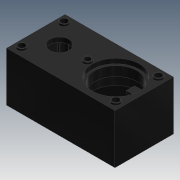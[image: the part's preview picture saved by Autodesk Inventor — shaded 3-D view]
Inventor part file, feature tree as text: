
AUTODESK INVENTOR PART (.ipt)
format: ipt  version: 2017 (Build 210142000, 142)  size: 245,760 bytes
history: native  units: mm
features: sketch x14, extrude x11, hole x3, projected_geometry x3, other x1, chamfer x1
ambient origin geometry x8: Origin, YZ Plane, XZ Plane, XY Plane, X Axis, Y Axis, Z Axis, Center Point
bodies: Body1 (feature_tree)
feature tree (33):
  other  "Твердое тело1"
  extrude  "Выдавливание1"  Depth=12.4mm
  extrude  "Выдавливание2"  Depth=23.0mm
  chamfer  "Фаска1"  Distance=10.5mm
  extrude  "Выдавливание3"  Depth=9.5mm TaperAngle=0.0deg
  extrude  "Выдавливание4"  Depth=1.5mm TaperAngle=45.0deg
  hole  "Отверстие1"  [1 undecoded]
  extrude  "Выдавливание5"  Depth=8.0mm
  extrude  "Выдавливание6"  Depth=1.0mm
  extrude  "Выдавливание7"  Depth=1.0mm
  extrude  "Выдавливание8"  Depth=4.0mm TaperAngle=0.0deg
  extrude  "Выдавливание9"  Depth=1.0mm TaperAngle=0.0deg
  extrude  "Выдавливание10"  Depth=10.0mm
  hole  "Отверстие2"  [1 undecoded]
  hole  "Отверстие3"  [1 undecoded]
  extrude  "Выдавливание11"  Depth=9.0mm
  sketch  "Эскиз1"
  sketch  "Эскиз2"
  projected_geometry  "Спроецированная петля1"
  sketch  "Эскиз3"
  sketch  "Эскиз4"
  sketch  "Эскиз5"
  sketch  "Эскиз6"
  sketch  "Эскиз7"
  projected_geometry  "Спроецированная петля2"
  sketch  "Эскиз8"
  projected_geometry  "Спроецированная петля3"
  sketch  "Эскиз9"
  sketch  "Эскиз10"
  sketch  "Эскиз11"
  sketch  "Эскиз12"
  sketch  "Эскиз13"
  sketch  "Эскиз14"
note: 3 required parameter values undecoded (feature->parameter linkage not recoverable at this tier; creation-order binding heuristic only, values carry confidence <= 0.55)
